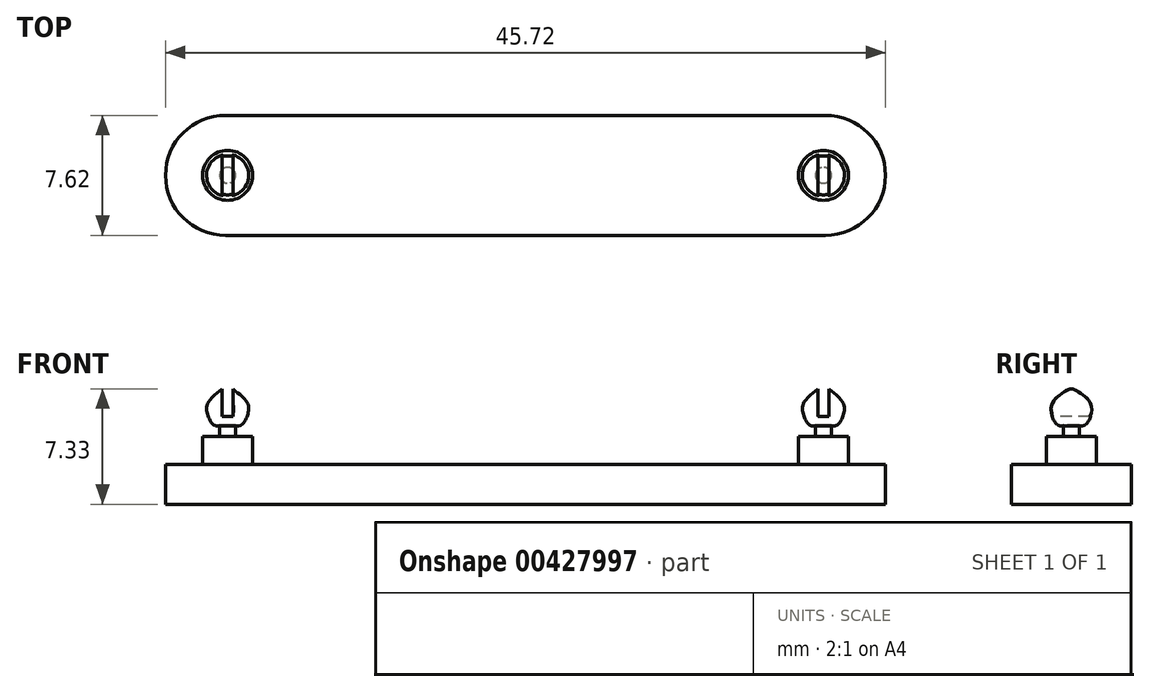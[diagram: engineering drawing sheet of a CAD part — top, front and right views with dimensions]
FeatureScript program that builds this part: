
annotation { "Feature Type Name" : "Feature", "Feature Type Description" : "" }
export const myFeature = defineFeature(function(context is Context, id is Id, definition is map)
    precondition{}
    {
        {
            var Q0;
            Q0=qCreatedBy(makeId("Top.planeOp"),FACE);
            var sketch = newSketch(context, id + "F0", { "sketchPlane" : qUnion([Q0])});
            skLineSegment(sketch, "E0", {"start": v(-19.05, 3.8) * mm, "end": v(0, 3.81) * mm});
            skLineSegment(sketch, "E1", {"start": v(0, -3.81) * mm, "end": v(-19.05, -3.81) * mm});
            skArc(sketch, "E2", {"start": v(-19.05, 3.8) * mm, "mid": v(-22.86, 0) * mm, "end": v(-19.05, -3.81) * mm});
            skLineSegment(sketch, "E3", {"start": v(-19.05, 3.8) * mm, "end": v(-19.05, -3.81) * mm});
            skLineSegment(sketch, "E4", {"start": v(0, 3.81) * mm, "end": v(0, -3.81) * mm});
            skSolve(sketch);
        }
        {
            var Q0;
            Q0=makeQuery(id+"F0.imprint","IMPRINT",FACE,{"disambiguationData":[TD([[makeQuery(id+"F0.imprint","IMPRINT",EDGE,{"derivedFrom":sQuery(id+"F0.wireOp",EDGE,"E0")}),-1.0]])]});
            var Q1;
            Q1=makeQuery(id+"F0.imprint","IMPRINT",FACE,{"disambiguationData":[TD([[makeQuery(id+"F0.imprint","IMPRINT",EDGE,{"derivedFrom":sQuery(id+"F0.wireOp",EDGE,"E2")}),1.0]])]});
            var Q2;
            Q2=makeQuery(id+"F0.imprint","IMPRINT",FACE,{"disambiguationData":[TD([[makeQuery(id+"F0.imprint","IMPRINT",EDGE,{"derivedFrom":sQuery(id+"F0.wireOp",EDGE,"mlqhV2yz-Mei3-w0GR-ghxX-rraUuCOPRNBw")}),1.0]])]});
            var Q3;
            {var subQ0=sQuery(id+"F0.wireOp",EDGE,"E1");Q3=makeQuery(id+"F0.imprint","IMPRINT",FACE,{"disambiguationData":[TD([[makeQuery(id+"F0.imprint","IMPRINT",EDGE,{"derivedFrom":subQ0}),-1.0]])]});}
            extrude(context, id + "F1", {"entities" : qUnion([Q0, Q1, Q2, Q3]), "depth" : 2.54 * mm});
        }
        {
            var Q0;
            Q0=makeQuery(id+"F1.opExtrude","CAP_FACE",FACE,{"disambiguationData":[OSD([sQuery(id+"F0.wireOp",EDGE,"E0"),sQuery(id+"F0.wireOp",EDGE,"E1"),sQuery(id+"F0.wireOp",EDGE,"E2"),sQuery(id+"F0.wireOp",EDGE,"mlqhV2yz-Mei3-w0GR-ghxX-rraUuCOPRNBw")])],"isStart":false});
            var sketch = newSketch(context, id + "F2", { "sketchPlane" : qUnion([Q0])});
            skPoint(sketch, "E5", {"position": v(-18.92, 0) * mm});
            skCircle(sketch, "E6", {"center": v(-18.92, 0) * mm, "radius": 1.59 * mm});
            skSolve(sketch);
        }
        {
            var Q0;
            Q0=makeQuery(id+"F2.imprint","IMPRINT",FACE,{"disambiguationData":[TD([[makeQuery(id+"F2.imprint","IMPRINT",EDGE,{"derivedFrom":sQuery(id+"F2.wireOp",EDGE,"E6")}),1.0]])]});
            extrude(context, id + "F3", {"entities" : qUnion([Q0]), "operationType" : NewBodyOperationType.ADD, "depth" : 1.78 * mm});
        }
        {
            var Q0;
            Q0=qCreatedBy(makeId("Front.planeOp"),FACE);
            var sketch = newSketch(context, id + "F4", { "sketchPlane" : qUnion([Q0])});
            skLineSegment(sketch, "E7.0.0", {"start": v(-20.5, 4.32) * mm, "end": v(-17.33, 4.32) * mm});
            skLineSegment(sketch, "E8", {"start": v(-18.92, 4.32) * mm, "end": v(-18.92, 7.65) * mm});
            skFitSpline(sketch, "E9", {"points": [v(-18.92, 7.65) * mm, v(-18.34, 7.13) * mm, v(-17.68, 6.47) * mm, v(-17.64, 5.7) * mm, v(-18.16, 4.98) * mm, v(-18.92, 5.44) * mm], "startDerivative": vector(2.82, -2.66) * mm, "endDerivative": vector(-3.9, 3.71) * mm});
            skSolve(sketch);
        }
        {
            var Q0;
            Q0=makeQuery(id+"F3.opExtrude","CAP_FACE",FACE,{"disambiguationData":[OSD([sQuery(id+"F2.wireOp",EDGE,"E6")])],"isStart":false});
            var sketch = newSketch(context, id + "F5", { "sketchPlane" : qUnion([Q0])});
            skCircle(sketch, "E10", {"center": v(-18.92, 0) * mm, "radius": 0.5 * mm});
            skSolve(sketch);
        }
        {
            var Q0;
            Q0=makeQuery(id+"F5.imprint","IMPRINT",FACE,{"disambiguationData":[TD([[makeQuery(id+"F5.imprint","IMPRINT",EDGE,{"derivedFrom":sQuery(id+"F5.wireOp",EDGE,"E10")}),1.0]])]});
            var Q1;
            Q1=makeQuery(id+"F5.imprint","IMPRINT",FACE,{"disambiguationData":[TD([[makeQuery(id+"F5.imprint","IMPRINT",EDGE,{"derivedFrom":sQuery(id+"F5.wireOp",EDGE,"IyrRUTJh-lQBa-heQx-TSyG-jGRHt6gB0DhX")}),1.0]])]});
            extrude(context, id + "F6", {"entities" : qUnion([Q0, Q1]), "operationType" : NewBodyOperationType.ADD, "depth" : 2.57 * mm});
        }
        {
            var Q0;
            {var subQ0=sQuery(id+"F4.wireOp",EDGE,"E9");Q0=makeQuery(id+"F4.imprint","IMPRINT",FACE,{"disambiguationData":[TD([[makeQuery(id+"F4.imprint","IMPRINT",EDGE,{"derivedFrom":subQ0}),-1.0]])]});}
            var Q1;
            Q1=sQuery(id+"F4.wireOp",EDGE,"E8");
            revolve(context, id + "F7", {"operationType" : NewBodyOperationType.ADD, "entities" : qUnion([Q0]), "axis" : qUnion([Q1]), "revolveType" : RevolveType.FULL});
        }
        {
            var Q0;
            {var subQ0=makeQuery(id+"F1.opExtrude","SWEPT_FACE",FACE,{"disambiguationData":[OSD([sQuery(id+"F0.wireOp",EDGE,"E1")])]});Q0=makeQuery(id+"F10.boolean.opBoolean","MERGE",FACE,{"derivedFrom":[subQ0,makeQuery(id+"F10.opPattern","COPY",FACE,{"derivedFrom":subQ0,"instanceName":"1"})]});}
            var sketch = newSketch(context, id + "F8", { "sketchPlane" : qUnion([Q0])});
            skLineSegment(sketch, "E11.bottom", {"start": v(-19.26, 8.54) * mm, "end": v(-18.58, 8.54) * mm});
            skLineSegment(sketch, "E11.top", {"start": v(-19.26, 5.59) * mm, "end": v(-18.58, 5.59) * mm});
            skLineSegment(sketch, "E11.left", {"start": v(-19.26, 8.54) * mm, "end": v(-19.26, 5.59) * mm});
            skLineSegment(sketch, "E11.right", {"start": v(-18.58, 8.54) * mm, "end": v(-18.58, 5.59) * mm});
            skLineSegment(sketch, "E12", {"start": v(-19.42, 4.32) * mm, "end": v(-19.42, 5.03) * mm});
            skLineSegment(sketch, "E13", {"start": v(-18.42, 5.03) * mm, "end": v(-18.42, 4.32) * mm});
            skLineSegment(sketch, "E14.0", {"start": v(-20.5, 4.32) * mm, "end": v(-17.33, 4.32) * mm});
            skLineSegment(sketch, "E15", {"start": v(-18.92, 5.59) * mm, "end": v(-18.92, 4.32) * mm});
            skSolve(sketch);
        }
        {
            var Q0;
            Q0=makeQuery(id+"F8.imprint","IMPRINT",FACE,{"disambiguationData":[TD([[makeQuery(id+"F8.imprint","IMPRINT",EDGE,{"derivedFrom":sQuery(id+"F8.wireOp",EDGE,"E11.bottom")}),-1.0]])]});
            extrude(context, id + "F9", {"entities" : qUnion([Q0]), "operationType" : NewBodyOperationType.REMOVE, "oppositeDirection" : true, "depth" : 25.4 * mm});
        }
        {
            var Q0;
            Q0=makeQuery(id+"F1.opExtrude","SWEPT_BODY",BODY,{"disambiguationData":[OSD([sQuery(id+"F0.wireOp",EDGE,"E0"),sQuery(id+"F0.wireOp",EDGE,"E1"),sQuery(id+"F0.wireOp",EDGE,"E2"),sQuery(id+"F0.wireOp",EDGE,"E4")])]});
            var Q1;
            Q1=qCreatedBy(makeId("Right.planeOp"),FACE);
            mirror(context, id + "F10", {"operationType" : NewBodyOperationType.ADD, "entities" : qUnion([Q0]), "mirrorPlane" : qUnion([Q1])});
        }
    });
